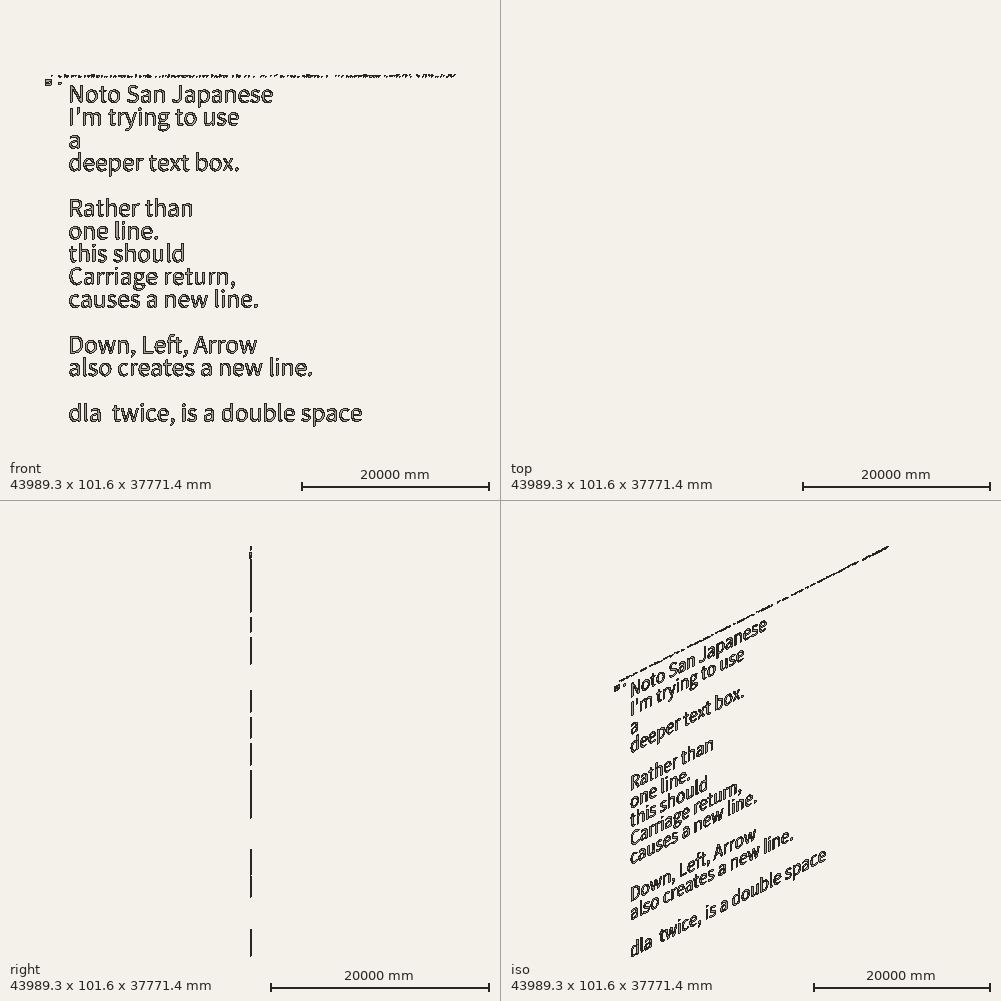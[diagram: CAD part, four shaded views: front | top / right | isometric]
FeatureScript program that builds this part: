
annotation { "Feature Type Name" : "Feature", "Feature Type Description" : "" }
export const myFeature = defineFeature(function(context is Context, id is Id, definition is map)
    precondition{}
    {
        {
            var Q0;
            Q0=qCreatedBy(makeId("Front.planeOp"),FACE);
            var sketch = newSketch(context, id + "F0", { "sketchPlane" : qUnion([Q0])});
            skLineSegment(sketch, "E0.bottom", {"start": v(144.98, -704.69) * mm, "end": v(832.17, -704.69) * mm});
            skLineSegment(sketch, "E0.top", {"start": v(144.98, -137.64) * mm, "end": v(832.17, -137.64) * mm});
            skLineSegment(sketch, "E0.left", {"start": v(144.98, -704.69) * mm, "end": v(144.98, -137.64) * mm});
            skLineSegment(sketch, "E0.right", {"start": v(832.17, -704.69) * mm, "end": v(832.17, -137.64) * mm});
            skPoint(sketch, "E0.middle", {"position": v(488.58, -421.16) * mm});
            skCircle(sketch, "E1", {"center": v(167.77, -191.42) * mm, "radius": 14.78 * mm});
            skCircle(sketch, "E2.0.1.0", {"center": v(183.37, -240.03) * mm, "radius": 14.78 * mm});
            skCircle(sketch, "E2.0.2.0", {"center": v(198.96, -288.64) * mm, "radius": 14.78 * mm});
            skCircle(sketch, "E2.0.3.0", {"center": v(214.56, -337.26) * mm, "radius": 14.78 * mm});
            skCircle(sketch, "E2.0.4.0", {"center": v(230.15, -385.87) * mm, "radius": 14.78 * mm});
            skCircle(sketch, "E2.0.5.0", {"center": v(245.75, -434.48) * mm, "radius": 14.78 * mm});
            skCircle(sketch, "E2.0.6.0", {"center": v(261.35, -483.1) * mm, "radius": 14.78 * mm});
            skCircle(sketch, "E2.0.7.0", {"center": v(276.94, -531.7) * mm, "radius": 14.78 * mm});
            skCircle(sketch, "E2.0.8.0", {"center": v(292.54, -580.32) * mm, "radius": 14.78 * mm});
            skCircle(sketch, "E2.0.9.0", {"center": v(308.14, -628.94) * mm, "radius": 14.78 * mm});
            skCircle(sketch, "E2.1.0.0", {"center": v(218.83, -191.42) * mm, "radius": 14.78 * mm});
            skCircle(sketch, "E2.1.1.0", {"center": v(234.43, -240.03) * mm, "radius": 14.78 * mm});
            skCircle(sketch, "E2.1.2.0", {"center": v(250.03, -288.64) * mm, "radius": 14.78 * mm});
            skCircle(sketch, "E2.1.3.0", {"center": v(265.62, -337.26) * mm, "radius": 14.78 * mm});
            skCircle(sketch, "E2.1.4.0", {"center": v(281.22, -385.87) * mm, "radius": 14.78 * mm});
            skCircle(sketch, "E2.1.5.0", {"center": v(296.82, -434.48) * mm, "radius": 14.78 * mm});
            skCircle(sketch, "E2.1.6.0", {"center": v(312.41, -483.1) * mm, "radius": 14.78 * mm});
            skCircle(sketch, "E2.1.7.0", {"center": v(328, -531.7) * mm, "radius": 14.78 * mm});
            skCircle(sketch, "E2.1.8.0", {"center": v(343.6, -580.32) * mm, "radius": 14.78 * mm});
            skCircle(sketch, "E2.1.9.0", {"center": v(359.2, -628.94) * mm, "radius": 14.78 * mm});
            skCircle(sketch, "E2.2.0.0", {"center": v(269.9, -191.42) * mm, "radius": 14.78 * mm});
            skCircle(sketch, "E2.2.1.0", {"center": v(285.5, -240.03) * mm, "radius": 14.78 * mm});
            skCircle(sketch, "E2.2.2.0", {"center": v(301.1, -288.64) * mm, "radius": 14.78 * mm});
            skCircle(sketch, "E2.2.3.0", {"center": v(316.69, -337.26) * mm, "radius": 14.78 * mm});
            skCircle(sketch, "E2.2.4.0", {"center": v(332.28, -385.87) * mm, "radius": 14.78 * mm});
            skCircle(sketch, "E2.2.5.0", {"center": v(347.88, -434.48) * mm, "radius": 14.78 * mm});
            skCircle(sketch, "E2.2.6.0", {"center": v(363.48, -483.1) * mm, "radius": 14.78 * mm});
            skCircle(sketch, "E2.2.7.0", {"center": v(379.07, -531.7) * mm, "radius": 14.78 * mm});
            skCircle(sketch, "E2.2.8.0", {"center": v(394.67, -580.32) * mm, "radius": 14.78 * mm});
            skCircle(sketch, "E2.2.9.0", {"center": v(410.27, -628.94) * mm, "radius": 14.78 * mm});
            skCircle(sketch, "E2.3.0.0", {"center": v(320.96, -191.42) * mm, "radius": 14.78 * mm});
            skCircle(sketch, "E2.3.1.0", {"center": v(336.56, -240.03) * mm, "radius": 14.78 * mm});
            skCircle(sketch, "E2.3.2.0", {"center": v(352.16, -288.64) * mm, "radius": 14.78 * mm});
            skCircle(sketch, "E2.3.3.0", {"center": v(367.75, -337.26) * mm, "radius": 14.78 * mm});
            skCircle(sketch, "E2.3.4.0", {"center": v(383.35, -385.87) * mm, "radius": 14.78 * mm});
            skCircle(sketch, "E2.3.5.0", {"center": v(398.94, -434.48) * mm, "radius": 14.78 * mm});
            skCircle(sketch, "E2.3.6.0", {"center": v(414.54, -483.1) * mm, "radius": 14.78 * mm});
            skCircle(sketch, "E2.3.7.0", {"center": v(430.14, -531.7) * mm, "radius": 14.78 * mm});
            skCircle(sketch, "E2.3.8.0", {"center": v(445.73, -580.32) * mm, "radius": 14.78 * mm});
            skCircle(sketch, "E2.3.9.0", {"center": v(461.33, -628.94) * mm, "radius": 14.78 * mm});
            skCircle(sketch, "E2.4.0.0", {"center": v(372.03, -191.42) * mm, "radius": 14.78 * mm});
            skCircle(sketch, "E2.4.1.0", {"center": v(387.62, -240.03) * mm, "radius": 14.78 * mm});
            skCircle(sketch, "E2.4.2.0", {"center": v(403.22, -288.64) * mm, "radius": 14.78 * mm});
            skCircle(sketch, "E2.4.3.0", {"center": v(418.82, -337.26) * mm, "radius": 14.78 * mm});
            skCircle(sketch, "E2.4.4.0", {"center": v(434.41, -385.87) * mm, "radius": 14.78 * mm});
            skCircle(sketch, "E2.4.5.0", {"center": v(450, -434.48) * mm, "radius": 14.78 * mm});
            skCircle(sketch, "E2.4.6.0", {"center": v(465.6, -483.1) * mm, "radius": 14.78 * mm});
            skCircle(sketch, "E2.4.7.0", {"center": v(481.2, -531.7) * mm, "radius": 14.78 * mm});
            skCircle(sketch, "E2.4.8.0", {"center": v(496.8, -580.32) * mm, "radius": 14.78 * mm});
            skCircle(sketch, "E2.4.9.0", {"center": v(512.4, -628.94) * mm, "radius": 14.78 * mm});
            skCircle(sketch, "E2.5.0.0", {"center": v(423.1, -191.42) * mm, "radius": 14.78 * mm});
            skCircle(sketch, "E2.5.1.0", {"center": v(438.69, -240.03) * mm, "radius": 14.78 * mm});
            skCircle(sketch, "E2.5.2.0", {"center": v(454.28, -288.64) * mm, "radius": 14.78 * mm});
            skCircle(sketch, "E2.5.3.0", {"center": v(469.88, -337.26) * mm, "radius": 14.78 * mm});
            skCircle(sketch, "E2.5.4.0", {"center": v(485.48, -385.87) * mm, "radius": 14.78 * mm});
            skCircle(sketch, "E2.5.5.0", {"center": v(501.07, -434.48) * mm, "radius": 14.78 * mm});
            skCircle(sketch, "E2.5.6.0", {"center": v(516.67, -483.1) * mm, "radius": 14.78 * mm});
            skCircle(sketch, "E2.5.7.0", {"center": v(532.27, -531.7) * mm, "radius": 14.78 * mm});
            skCircle(sketch, "E2.5.8.0", {"center": v(547.86, -580.32) * mm, "radius": 14.78 * mm});
            skCircle(sketch, "E2.5.9.0", {"center": v(563.46, -628.94) * mm, "radius": 14.78 * mm});
            skCircle(sketch, "E2.6.0.0", {"center": v(474.16, -191.42) * mm, "radius": 14.78 * mm});
            skCircle(sketch, "E2.6.1.0", {"center": v(489.75, -240.03) * mm, "radius": 14.78 * mm});
            skCircle(sketch, "E2.6.2.0", {"center": v(505.35, -288.64) * mm, "radius": 14.78 * mm});
            skCircle(sketch, "E2.6.3.0", {"center": v(520.95, -337.26) * mm, "radius": 14.78 * mm});
            skCircle(sketch, "E2.6.4.0", {"center": v(536.54, -385.87) * mm, "radius": 14.78 * mm});
            skCircle(sketch, "E2.6.5.0", {"center": v(552.14, -434.48) * mm, "radius": 14.78 * mm});
            skCircle(sketch, "E2.6.6.0", {"center": v(567.74, -483.1) * mm, "radius": 14.78 * mm});
            skCircle(sketch, "E2.6.7.0", {"center": v(583.33, -531.7) * mm, "radius": 14.78 * mm});
            skCircle(sketch, "E2.6.8.0", {"center": v(598.93, -580.32) * mm, "radius": 14.78 * mm});
            skCircle(sketch, "E2.6.9.0", {"center": v(614.52, -628.94) * mm, "radius": 14.78 * mm});
            skCircle(sketch, "E2.7.0.0", {"center": v(525.22, -191.42) * mm, "radius": 14.78 * mm});
            skCircle(sketch, "E2.7.1.0", {"center": v(540.82, -240.03) * mm, "radius": 14.78 * mm});
            skCircle(sketch, "E2.7.2.0", {"center": v(556.41, -288.64) * mm, "radius": 14.78 * mm});
            skCircle(sketch, "E2.7.3.0", {"center": v(572.01, -337.26) * mm, "radius": 14.78 * mm});
            skCircle(sketch, "E2.7.4.0", {"center": v(587.6, -385.87) * mm, "radius": 14.78 * mm});
            skCircle(sketch, "E2.7.5.0", {"center": v(603.2, -434.48) * mm, "radius": 14.78 * mm});
            skCircle(sketch, "E2.7.6.0", {"center": v(618.8, -483.1) * mm, "radius": 14.78 * mm});
            skCircle(sketch, "E2.7.7.0", {"center": v(634.4, -531.7) * mm, "radius": 14.78 * mm});
            skCircle(sketch, "E2.7.8.0", {"center": v(650, -580.32) * mm, "radius": 14.78 * mm});
            skCircle(sketch, "E2.7.9.0", {"center": v(665.59, -628.94) * mm, "radius": 14.78 * mm});
            skCircle(sketch, "E2.8.0.0", {"center": v(576.29, -191.42) * mm, "radius": 14.78 * mm});
            skCircle(sketch, "E2.8.1.0", {"center": v(591.88, -240.03) * mm, "radius": 14.78 * mm});
            skCircle(sketch, "E2.8.2.0", {"center": v(607.48, -288.64) * mm, "radius": 14.78 * mm});
            skCircle(sketch, "E2.8.3.0", {"center": v(623.07, -337.26) * mm, "radius": 14.78 * mm});
            skCircle(sketch, "E2.8.4.0", {"center": v(638.67, -385.87) * mm, "radius": 14.78 * mm});
            skCircle(sketch, "E2.8.5.0", {"center": v(654.27, -434.48) * mm, "radius": 14.78 * mm});
            skCircle(sketch, "E2.8.6.0", {"center": v(669.86, -483.1) * mm, "radius": 14.78 * mm});
            skCircle(sketch, "E2.8.7.0", {"center": v(685.46, -531.7) * mm, "radius": 14.78 * mm});
            skCircle(sketch, "E2.8.8.0", {"center": v(701.06, -580.32) * mm, "radius": 14.78 * mm});
            skCircle(sketch, "E2.8.9.0", {"center": v(716.65, -628.94) * mm, "radius": 14.78 * mm});
            skCircle(sketch, "E2.9.0.0", {"center": v(627.35, -191.42) * mm, "radius": 14.78 * mm});
            skCircle(sketch, "E2.9.1.0", {"center": v(642.95, -240.03) * mm, "radius": 14.78 * mm});
            skCircle(sketch, "E2.9.2.0", {"center": v(658.54, -288.64) * mm, "radius": 14.78 * mm});
            skCircle(sketch, "E2.9.3.0", {"center": v(674.14, -337.26) * mm, "radius": 14.78 * mm});
            skCircle(sketch, "E2.9.4.0", {"center": v(689.74, -385.87) * mm, "radius": 14.78 * mm});
            skCircle(sketch, "E2.9.5.0", {"center": v(705.33, -434.48) * mm, "radius": 14.78 * mm});
            skCircle(sketch, "E2.9.6.0", {"center": v(720.93, -483.1) * mm, "radius": 14.78 * mm});
            skCircle(sketch, "E2.9.7.0", {"center": v(736.53, -531.7) * mm, "radius": 14.78 * mm});
            skCircle(sketch, "E2.9.8.0", {"center": v(752.12, -580.32) * mm, "radius": 14.78 * mm});
            skCircle(sketch, "E2.9.9.0", {"center": v(767.72, -628.94) * mm, "radius": 14.78 * mm});
            skLineSegment(sketch, "E2.direction1", {"start": v(167.77, -191.42) * mm, "end": v(218.83, -191.42) * mm, "construction": true});
            skLineSegment(sketch, "E2.direction2", {"start": v(167.77, -191.42) * mm, "end": v(183.37, -240.03) * mm, "construction": true});
            skSolve(sketch);
        }
        {
            var Q0;
            Q0=makeQuery(id+"F0.imprint","IMPRINT",FACE,{"disambiguationData":[TD([[makeQuery(id+"F0.imprint","IMPRINT",EDGE,{"derivedFrom":sQuery(id+"F0.wireOp",EDGE,"E0.bottom")}),1.0]])]});
            extrude(context, id + "F1", {"entities" : qUnion([Q0]), "depth" : 101.6 * mm});
        }
        {
            var Q0;
            Q0=qCreatedBy(makeId("Front.planeOp"),FACE);
            var sketch = newSketch(context, id + "F2", { "sketchPlane" : qUnion([Q0])});
            skCircle(sketch, "E3", {"center": v(1587.58, -652.03) * mm, "radius": 3.18 * mm});
            skCircle(sketch, "E4.0.1.0", {"center": v(1587.58, -626.63) * mm, "radius": 3.18 * mm});
            skCircle(sketch, "E4.0.2.0", {"center": v(1587.58, -601.23) * mm, "radius": 3.18 * mm});
            skCircle(sketch, "E4.0.3.0", {"center": v(1587.58, -575.83) * mm, "radius": 3.18 * mm});
            skCircle(sketch, "E4.0.4.0", {"center": v(1587.58, -550.43) * mm, "radius": 3.18 * mm});
            skCircle(sketch, "E4.0.5.0", {"center": v(1587.58, -525.03) * mm, "radius": 3.18 * mm});
            skCircle(sketch, "E4.0.6.0", {"center": v(1587.58, -499.63) * mm, "radius": 3.18 * mm});
            skCircle(sketch, "E4.0.7.0", {"center": v(1587.58, -474.23) * mm, "radius": 3.18 * mm});
            skCircle(sketch, "E4.0.8.0", {"center": v(1587.58, -448.83) * mm, "radius": 3.18 * mm});
            skCircle(sketch, "E4.0.9.0", {"center": v(1587.58, -423.43) * mm, "radius": 3.18 * mm});
            skCircle(sketch, "E4.1.0.0", {"center": v(1612.98, -652.03) * mm, "radius": 3.18 * mm});
            skCircle(sketch, "E4.1.1.0", {"center": v(1612.98, -626.63) * mm, "radius": 3.18 * mm});
            skCircle(sketch, "E4.1.2.0", {"center": v(1612.98, -601.23) * mm, "radius": 3.18 * mm});
            skCircle(sketch, "E4.1.3.0", {"center": v(1612.98, -575.83) * mm, "radius": 3.18 * mm});
            skCircle(sketch, "E4.1.4.0", {"center": v(1612.98, -550.43) * mm, "radius": 3.18 * mm});
            skCircle(sketch, "E4.1.5.0", {"center": v(1612.98, -525.03) * mm, "radius": 3.18 * mm});
            skCircle(sketch, "E4.1.6.0", {"center": v(1612.98, -499.63) * mm, "radius": 3.18 * mm});
            skCircle(sketch, "E4.1.7.0", {"center": v(1612.98, -474.23) * mm, "radius": 3.18 * mm});
            skCircle(sketch, "E4.1.8.0", {"center": v(1612.98, -448.83) * mm, "radius": 3.18 * mm});
            skCircle(sketch, "E4.1.9.0", {"center": v(1612.98, -423.43) * mm, "radius": 3.18 * mm});
            skCircle(sketch, "E4.2.0.0", {"center": v(1638.38, -652.03) * mm, "radius": 3.18 * mm});
            skCircle(sketch, "E4.2.1.0", {"center": v(1638.38, -626.63) * mm, "radius": 3.18 * mm});
            skCircle(sketch, "E4.2.2.0", {"center": v(1638.38, -601.23) * mm, "radius": 3.18 * mm});
            skCircle(sketch, "E4.2.3.0", {"center": v(1638.38, -575.83) * mm, "radius": 3.18 * mm});
            skCircle(sketch, "E4.2.4.0", {"center": v(1638.38, -550.43) * mm, "radius": 3.18 * mm});
            skCircle(sketch, "E4.2.5.0", {"center": v(1638.38, -525.03) * mm, "radius": 3.18 * mm});
            skCircle(sketch, "E4.2.6.0", {"center": v(1638.38, -499.63) * mm, "radius": 3.18 * mm});
            skCircle(sketch, "E4.2.7.0", {"center": v(1638.38, -474.23) * mm, "radius": 3.18 * mm});
            skCircle(sketch, "E4.2.8.0", {"center": v(1638.38, -448.83) * mm, "radius": 3.18 * mm});
            skCircle(sketch, "E4.2.9.0", {"center": v(1638.38, -423.43) * mm, "radius": 3.18 * mm});
            skCircle(sketch, "E4.3.0.0", {"center": v(1663.78, -652.03) * mm, "radius": 3.18 * mm});
            skCircle(sketch, "E4.3.1.0", {"center": v(1663.78, -626.63) * mm, "radius": 3.18 * mm});
            skCircle(sketch, "E4.3.2.0", {"center": v(1663.78, -601.23) * mm, "radius": 3.18 * mm});
            skCircle(sketch, "E4.3.3.0", {"center": v(1663.78, -575.83) * mm, "radius": 3.18 * mm});
            skCircle(sketch, "E4.3.4.0", {"center": v(1663.78, -550.43) * mm, "radius": 3.18 * mm});
            skCircle(sketch, "E4.3.5.0", {"center": v(1663.78, -525.03) * mm, "radius": 3.18 * mm});
            skCircle(sketch, "E4.3.6.0", {"center": v(1663.78, -499.63) * mm, "radius": 3.18 * mm});
            skCircle(sketch, "E4.3.7.0", {"center": v(1663.78, -474.23) * mm, "radius": 3.18 * mm});
            skCircle(sketch, "E4.3.8.0", {"center": v(1663.78, -448.83) * mm, "radius": 3.18 * mm});
            skCircle(sketch, "E4.3.9.0", {"center": v(1663.78, -423.43) * mm, "radius": 3.18 * mm});
            skCircle(sketch, "E4.4.0.0", {"center": v(1689.18, -652.03) * mm, "radius": 3.18 * mm});
            skCircle(sketch, "E4.4.1.0", {"center": v(1689.18, -626.63) * mm, "radius": 3.18 * mm});
            skCircle(sketch, "E4.4.2.0", {"center": v(1689.18, -601.23) * mm, "radius": 3.18 * mm});
            skCircle(sketch, "E4.4.3.0", {"center": v(1689.18, -575.83) * mm, "radius": 3.18 * mm});
            skCircle(sketch, "E4.4.4.0", {"center": v(1689.18, -550.43) * mm, "radius": 3.18 * mm});
            skCircle(sketch, "E4.4.5.0", {"center": v(1689.18, -525.03) * mm, "radius": 3.18 * mm});
            skCircle(sketch, "E4.4.6.0", {"center": v(1689.18, -499.63) * mm, "radius": 3.18 * mm});
            skCircle(sketch, "E4.4.7.0", {"center": v(1689.18, -474.23) * mm, "radius": 3.18 * mm});
            skCircle(sketch, "E4.4.8.0", {"center": v(1689.18, -448.83) * mm, "radius": 3.18 * mm});
            skCircle(sketch, "E4.4.9.0", {"center": v(1689.18, -423.43) * mm, "radius": 3.18 * mm});
            skCircle(sketch, "E4.5.0.0", {"center": v(1714.58, -652.03) * mm, "radius": 3.18 * mm});
            skCircle(sketch, "E4.5.1.0", {"center": v(1714.58, -626.63) * mm, "radius": 3.18 * mm});
            skCircle(sketch, "E4.5.2.0", {"center": v(1714.58, -601.23) * mm, "radius": 3.18 * mm});
            skCircle(sketch, "E4.5.3.0", {"center": v(1714.58, -575.83) * mm, "radius": 3.18 * mm});
            skCircle(sketch, "E4.5.4.0", {"center": v(1714.58, -550.43) * mm, "radius": 3.18 * mm});
            skCircle(sketch, "E4.5.5.0", {"center": v(1714.58, -525.03) * mm, "radius": 3.18 * mm});
            skCircle(sketch, "E4.5.6.0", {"center": v(1714.58, -499.63) * mm, "radius": 3.18 * mm});
            skCircle(sketch, "E4.5.7.0", {"center": v(1714.58, -474.23) * mm, "radius": 3.18 * mm});
            skCircle(sketch, "E4.5.8.0", {"center": v(1714.58, -448.83) * mm, "radius": 3.18 * mm});
            skCircle(sketch, "E4.5.9.0", {"center": v(1714.58, -423.43) * mm, "radius": 3.18 * mm});
            skCircle(sketch, "E4.6.0.0", {"center": v(1739.98, -652.03) * mm, "radius": 3.18 * mm});
            skCircle(sketch, "E4.6.1.0", {"center": v(1739.98, -626.63) * mm, "radius": 3.18 * mm});
            skCircle(sketch, "E4.6.2.0", {"center": v(1739.98, -601.23) * mm, "radius": 3.18 * mm});
            skCircle(sketch, "E4.6.3.0", {"center": v(1739.98, -575.83) * mm, "radius": 3.18 * mm});
            skCircle(sketch, "E4.6.4.0", {"center": v(1739.98, -550.43) * mm, "radius": 3.18 * mm});
            skCircle(sketch, "E4.6.5.0", {"center": v(1739.98, -525.03) * mm, "radius": 3.18 * mm});
            skCircle(sketch, "E4.6.6.0", {"center": v(1739.98, -499.63) * mm, "radius": 3.18 * mm});
            skCircle(sketch, "E4.6.7.0", {"center": v(1739.98, -474.23) * mm, "radius": 3.18 * mm});
            skCircle(sketch, "E4.6.8.0", {"center": v(1739.98, -448.83) * mm, "radius": 3.18 * mm});
            skCircle(sketch, "E4.6.9.0", {"center": v(1739.98, -423.43) * mm, "radius": 3.18 * mm});
            skCircle(sketch, "E4.7.0.0", {"center": v(1765.38, -652.03) * mm, "radius": 3.18 * mm});
            skCircle(sketch, "E4.7.1.0", {"center": v(1765.38, -626.63) * mm, "radius": 3.18 * mm});
            skCircle(sketch, "E4.7.2.0", {"center": v(1765.38, -601.23) * mm, "radius": 3.18 * mm});
            skCircle(sketch, "E4.7.3.0", {"center": v(1765.38, -575.83) * mm, "radius": 3.18 * mm});
            skCircle(sketch, "E4.7.4.0", {"center": v(1765.38, -550.43) * mm, "radius": 3.18 * mm});
            skCircle(sketch, "E4.7.5.0", {"center": v(1765.38, -525.03) * mm, "radius": 3.18 * mm});
            skCircle(sketch, "E4.7.6.0", {"center": v(1765.38, -499.63) * mm, "radius": 3.18 * mm});
            skCircle(sketch, "E4.7.7.0", {"center": v(1765.38, -474.23) * mm, "radius": 3.18 * mm});
            skCircle(sketch, "E4.7.8.0", {"center": v(1765.38, -448.83) * mm, "radius": 3.18 * mm});
            skCircle(sketch, "E4.7.9.0", {"center": v(1765.38, -423.43) * mm, "radius": 3.18 * mm});
            skCircle(sketch, "E4.8.0.0", {"center": v(1790.78, -652.03) * mm, "radius": 3.18 * mm});
            skCircle(sketch, "E4.8.1.0", {"center": v(1790.78, -626.63) * mm, "radius": 3.18 * mm});
            skCircle(sketch, "E4.8.2.0", {"center": v(1790.78, -601.23) * mm, "radius": 3.18 * mm});
            skCircle(sketch, "E4.8.3.0", {"center": v(1790.78, -575.83) * mm, "radius": 3.18 * mm});
            skCircle(sketch, "E4.8.4.0", {"center": v(1790.78, -550.43) * mm, "radius": 3.18 * mm});
            skCircle(sketch, "E4.8.5.0", {"center": v(1790.78, -525.03) * mm, "radius": 3.18 * mm});
            skCircle(sketch, "E4.8.6.0", {"center": v(1790.78, -499.63) * mm, "radius": 3.18 * mm});
            skCircle(sketch, "E4.8.7.0", {"center": v(1790.78, -474.23) * mm, "radius": 3.18 * mm});
            skCircle(sketch, "E4.8.8.0", {"center": v(1790.78, -448.83) * mm, "radius": 3.18 * mm});
            skCircle(sketch, "E4.8.9.0", {"center": v(1790.78, -423.43) * mm, "radius": 3.18 * mm});
            skCircle(sketch, "E4.9.0.0", {"center": v(1816.18, -652.03) * mm, "radius": 3.18 * mm});
            skCircle(sketch, "E4.9.1.0", {"center": v(1816.18, -626.63) * mm, "radius": 3.18 * mm});
            skCircle(sketch, "E4.9.2.0", {"center": v(1816.18, -601.23) * mm, "radius": 3.18 * mm});
            skCircle(sketch, "E4.9.3.0", {"center": v(1816.18, -575.83) * mm, "radius": 3.18 * mm});
            skCircle(sketch, "E4.9.4.0", {"center": v(1816.18, -550.43) * mm, "radius": 3.18 * mm});
            skCircle(sketch, "E4.9.5.0", {"center": v(1816.18, -525.03) * mm, "radius": 3.18 * mm});
            skCircle(sketch, "E4.9.6.0", {"center": v(1816.18, -499.63) * mm, "radius": 3.18 * mm});
            skCircle(sketch, "E4.9.7.0", {"center": v(1816.18, -474.23) * mm, "radius": 3.18 * mm});
            skCircle(sketch, "E4.9.8.0", {"center": v(1816.18, -448.83) * mm, "radius": 3.18 * mm});
            skCircle(sketch, "E4.9.9.0", {"center": v(1816.18, -423.43) * mm, "radius": 3.18 * mm});
            skLineSegment(sketch, "E4.direction1", {"start": v(1587.58, -652.03) * mm, "end": v(1612.98, -652.03) * mm, "construction": true});
            skLineSegment(sketch, "E4.direction2", {"start": v(1587.58, -652.03) * mm, "end": v(1587.58, -626.63) * mm, "construction": true});
            skLineSegment(sketch, "E5.bottom", {"start": v(1562.18, -398.03) * mm, "end": v(1841.58, -398.03) * mm});
            skLineSegment(sketch, "E5.top", {"start": v(1562.18, -677.43) * mm, "end": v(1841.58, -677.43) * mm});
            skLineSegment(sketch, "E5.left", {"start": v(1562.18, -398.03) * mm, "end": v(1562.18, -677.43) * mm});
            skLineSegment(sketch, "E5.right", {"start": v(1841.58, -398.03) * mm, "end": v(1841.58, -677.43) * mm});
            skSolve(sketch);
        }
        {
            var Q0;
            Q0 = qSketchRegion(id + "F2", true);
            extrude(context, id + "F3", {"entities" : qUnion([Q0]), "depth" : 12.7 * mm});
        }
        {
            var Q0;
            Q0=qCreatedBy(makeId("Front.planeOp"),FACE);
            var sketch = newSketch(context, id + "F4", { "sketchPlane" : qUnion([Q0])});
            skText(sketch, "E6", { "text": "Arimo: This is what I should have done 30 years ago! Thanks Liz, for the acknowledgment of the word! Now I can\'t get this from my \" Top of Mind\", list! Guess what, I have another mind worm developed from an employee of O P R A H. WHAT A PILE OF EXCR", "fontName": "Arimo-Regular.ttf"});
            const initialGuessF4  = {"E6": [0.78571, 0.15384, 1, 0, 0.27151]};
            skSetInitialGuess(sketch, initialGuessF4);
            skSolve(sketch);
        }
        {
            var Q0;
            Q0 = qSketchRegion(id + "F4", true);
            extrude(context, id + "F5", {"entities" : qUnion([Q0]), "depth" : 25.4 * mm});
        }
        {
            var Q0;
            Q0=qCreatedBy(makeId("Front.planeOp"),FACE);
            var sketch = newSketch(context, id + "F6", { "sketchPlane" : qUnion([Q0])});
            skText(sketch, "E7", { "text": "Noto San Japanese\nI\'m trying to use\na \ndeeper text box.\n\nRather than \none line.\nthis should\nCarriage return, \ncauses a new line.\n\nDown, Left, Arrow \nalso creates a new line.\n\ndla  twice, is a double space", "fontName": "NotoSansCJKjp-Regular.otf"});
            const initialGuessF6  = {"E7": [2.6076, -2.58726, 1, 0, 1.75873]};
            skSetInitialGuess(sketch, initialGuessF6);
            skSolve(sketch);
        }
        {
            var Q0;
            Q0 = qSketchRegion(id + "F6", true);
            var Q1;
            Q1 = qSketchRegion(id + "F6", true);
            extrude(context, id + "F7", {"entities" : qUnion([Q0, Q1]), "depth" : 25.4 * mm});
        }
    });
